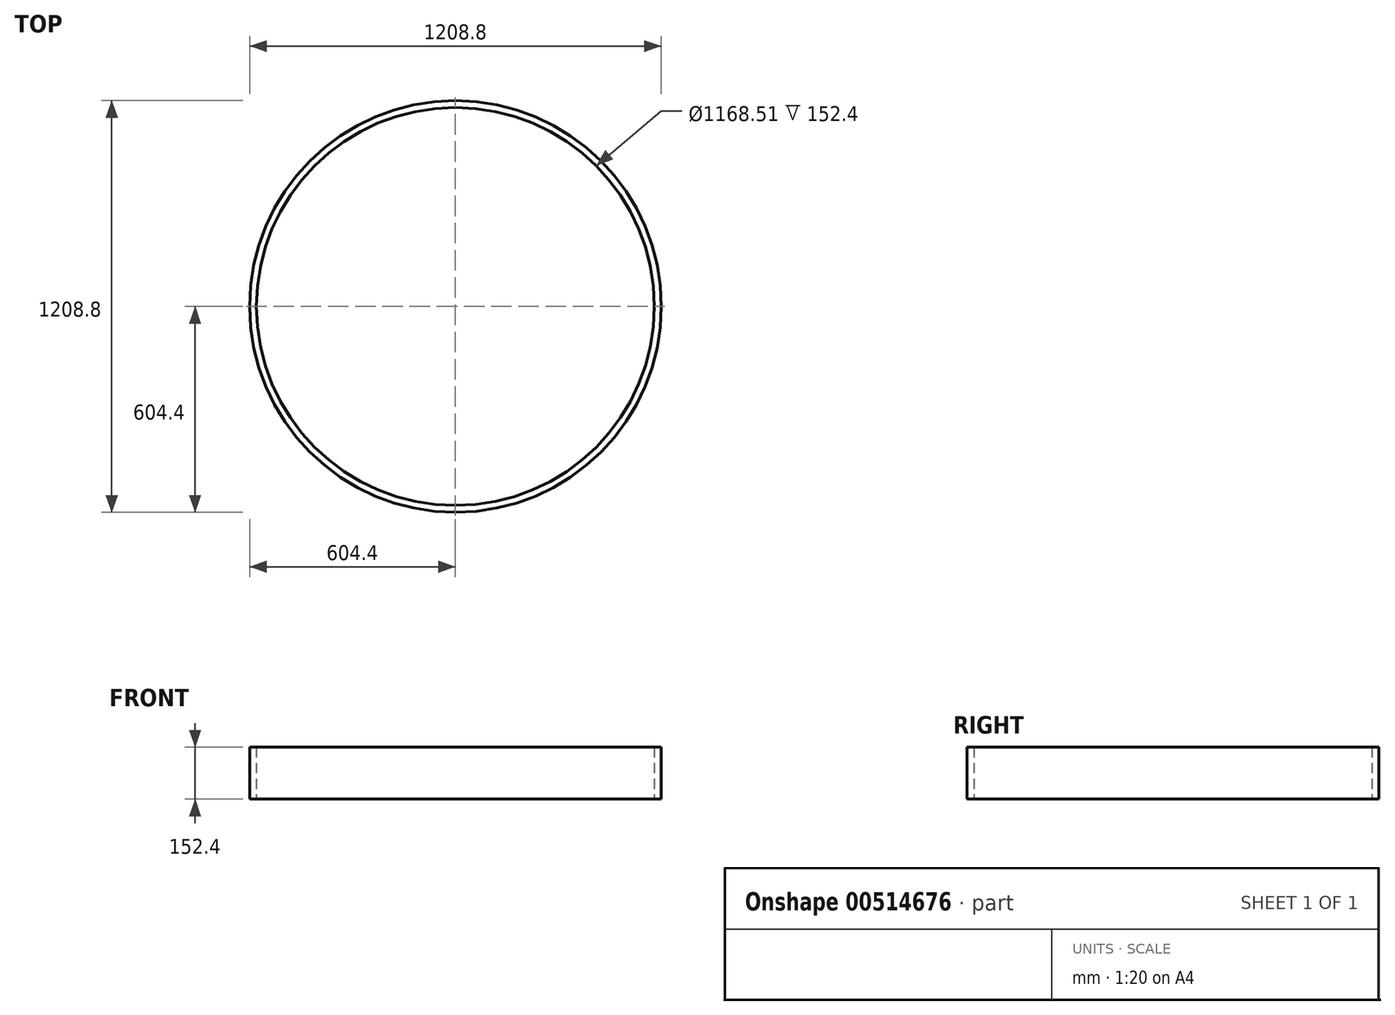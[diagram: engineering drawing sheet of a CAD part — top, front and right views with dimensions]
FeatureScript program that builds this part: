
annotation { "Feature Type Name" : "Feature", "Feature Type Description" : "" }
export const myFeature = defineFeature(function(context is Context, id is Id, definition is map)
    precondition{}
    {
        {
            var Q0;
            Q0=qCreatedBy(makeId("Top.planeOp"),FACE);
            var sketch = newSketch(context, id + "F0", { "sketchPlane" : qUnion([Q0])});
            skCircle(sketch, "E0", {"center": v(0, 0) * mm, "radius": 604.4 * mm});
            skCircle(sketch, "E1", {"center": v(0, 0) * mm, "radius": 584.26 * mm});
            skArc(sketch, "E2", {"start": v(-2050.35, -897.1) * mm, "mid": v(-1868.68, -1335.69) * mm, "end": v(-1430.08, -1517.36) * mm});
            skLineSegment(sketch, "E3", {"start": v(-2050.35, -897.1) * mm, "end": v(-2050.35, -1517.36) * mm});
            skLineSegment(sketch, "E4", {"start": v(-1430.08, -1517.36) * mm, "end": v(-1430.08, -1662.18) * mm});
            skLineSegment(sketch, "E5", {"start": v(-2050.35, -1517.36) * mm, "end": v(-2050.35, -1669.76) * mm});
            skSolve(sketch);
        }
        {
            var Q0;
            Q0=makeQuery(id+"F0.imprint","IMPRINT",FACE,{"disambiguationData":[TD([[makeQuery(id+"F0.imprint","IMPRINT",EDGE,{"derivedFrom":sQuery(id+"F0.wireOp",EDGE,"E0")}),1.0]])]});
            extrude(context, id + "F1", {"entities" : qUnion([Q0]), "depth" : 152.4 * mm, "offsetDistance" : 25.4 * mm});
        }
    });
